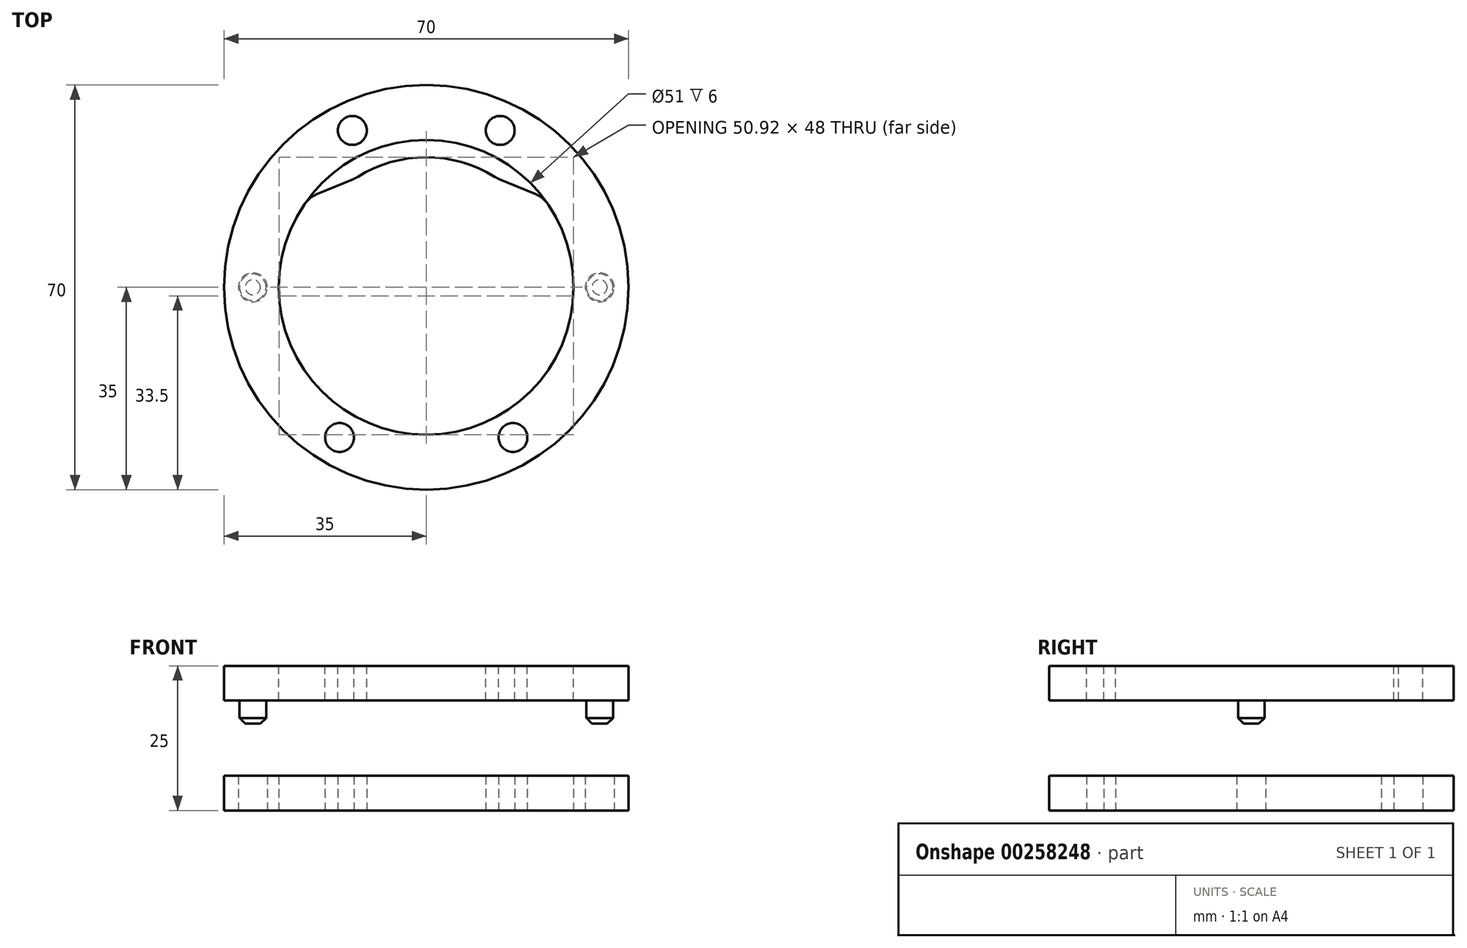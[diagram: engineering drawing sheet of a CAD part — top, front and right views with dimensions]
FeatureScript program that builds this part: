
annotation { "Feature Type Name" : "Feature", "Feature Type Description" : "" }
export const myFeature = defineFeature(function(context is Context, id is Id, definition is map)
    precondition{}
    {
        {
            var Q0;
            Q0=qCreatedBy(makeId("Top.planeOp"),FACE);
            var sketch = newSketch(context, id + "F0", { "sketchPlane" : qUnion([Q0])});
            skCircle(sketch, "E0", {"center": v(0, 0) * mm, "radius": 35 * mm});
            skArc(sketch, "E1", {"start": v(-21.1, 14.33) * mm, "mid": v(0, -25.5) * mm, "end": v(21.1, 14.33) * mm});
            skCircle(sketch, "E2", {"center": v(-15, 25.98) * mm, "radius": 2.5 * mm, "construction": true});
            skCircle(sketch, "E3", {"center": v(0, 0) * mm, "radius": 30 * mm, "construction": true});
            skCircle(sketch, "E4.1.0", {"center": v(-30, 0) * mm, "radius": 2.5 * mm});
            skCircle(sketch, "E4.2.0", {"center": v(-15, -25.98) * mm, "radius": 2.5 * mm});
            skCircle(sketch, "E5.1.3.0", {"center": v(15, -25.98) * mm, "radius": 2.5 * mm});
            skCircle(sketch, "E5.1.4.0", {"center": v(30, 0) * mm, "radius": 2.5 * mm});
            skCircle(sketch, "E5.1.5.0", {"center": v(15, 25.98) * mm, "radius": 2.5 * mm, "construction": true});
            skLineSegment(sketch, "E6", {"start": v(-18.87, 16.14) * mm, "end": v(-12.63, 18.72) * mm});
            skArc(sketch, "E7", {"start": v(11.9, 19.1) * mm, "mid": v(0, 22.5) * mm, "end": v(-11.9, 19.1) * mm});
            skLineSegment(sketch, "E8", {"start": v(18.87, 16.14) * mm, "end": v(12.63, 18.72) * mm});
            skPoint(sketch, "E9.visualSharp", {"position": v(20.17, 15.6) * mm});
            skArc(sketch, "E9.filletArc", {"start": v(21.1, 14.33) * mm, "mid": v(20.11, 15.4) * mm, "end": v(18.87, 16.14) * mm});
            skPoint(sketch, "E10.visualSharp", {"position": v(-12.23, 18.89) * mm});
            skArc(sketch, "E10.filletArc", {"start": v(-12.63, 18.72) * mm, "mid": v(-12.26, 18.9) * mm, "end": v(-11.9, 19.1) * mm});
            skPoint(sketch, "E11.visualSharp", {"position": v(-20.17, 15.6) * mm});
            skArc(sketch, "E11.filletArc", {"start": v(-18.87, 16.14) * mm, "mid": v(-20.11, 15.4) * mm, "end": v(-21.1, 14.33) * mm});
            skPoint(sketch, "E12.visualSharp", {"position": v(12.23, 18.89) * mm});
            skArc(sketch, "E12.filletArc", {"start": v(11.9, 19.1) * mm, "mid": v(12.26, 18.9) * mm, "end": v(12.63, 18.72) * mm});
            skCircle(sketch, "E13", {"center": v(12.78, 27.14) * mm, "radius": 2.5 * mm});
            skCircle(sketch, "E14", {"center": v(-12.78, 27.14) * mm, "radius": 2.5 * mm});
            skSolve(sketch);
        }
        {
            var Q0;
            Q0 = qSketchRegion(id + "F0", true);
            extrude(context, id + "F1", {"entities" : qUnion([Q0]), "depth" : 6 * mm});
        }
        {
            var Q0;
            Q0=qCreatedBy(makeId("Top.planeOp"),FACE);
            cPlane(context, id + "F2", {"entities" : qUnion([Q0]), "cplaneType" : CPlaneType.OFFSET, "offset" : 25 * mm, "width" : 150 * mm, "height" : 150 * mm});
        }
        {
            var Q0;
            Q0=qCreatedBy(id+"F2.planeOp",FACE);
            var sketch = newSketch(context, id + "F3", { "sketchPlane" : qUnion([Q0])});
            skCircle(sketch, "E15.0", {"center": v(0, 0) * mm, "radius": 25.5 * mm});
            skCircle(sketch, "E15.1", {"center": v(0, 0) * mm, "radius": 35 * mm});
            skCircle(sketch, "E16.3", {"center": v(-15, -25.98) * mm, "radius": 2.5 * mm});
            skCircle(sketch, "E17.0", {"center": v(12.78, 27.14) * mm, "radius": 2.5 * mm});
            skCircle(sketch, "E17.1", {"center": v(-12.78, 27.14) * mm, "radius": 2.5 * mm});
            skCircle(sketch, "E18.0", {"center": v(15, -25.98) * mm, "radius": 2.5 * mm});
            skSolve(sketch);
        }
        {
            var Q0;
            Q0 = qSketchRegion(id + "F3", true);
            extrude(context, id + "F4", {"entities" : qUnion([Q0]), "oppositeDirection" : true, "depth" : 6 * mm});
        }
        {
            var Q0;
            Q0=makeQuery(id+"F4.opExtrude","CAP_FACE",FACE,{"disambiguationData":[OSD([sQuery(id+"F3.wireOp",EDGE,"E15.0"),sQuery(id+"F3.wireOp",EDGE,"E15.1")])],"isStart":false});
            var sketch = newSketch(context, id + "F5", { "sketchPlane" : qUnion([Q0])});
            skCircle(sketch, "E19.0", {"center": v(30, 0) * mm, "radius": 2.5 * mm, "construction": true});
            skCircle(sketch, "E19.1", {"center": v(-30, 0) * mm, "radius": 2.5 * mm, "construction": true});
            skCircle(sketch, "E20.0", {"center": v(-30, 0) * mm, "radius": 2.3 * mm});
            skCircle(sketch, "E21.0", {"center": v(30, 0) * mm, "radius": 2.3 * mm});
            skSolve(sketch);
        }
        {
            var Q0;
            Q0 = qSketchRegion(id + "F5", true);
            extrude(context, id + "F6", {"entities" : qUnion([Q0]), "operationType" : NewBodyOperationType.ADD, "depth" : 4 * mm});
        }
        {
            var Q0;
            Q0=makeQuery(id+"F6.opExtrude","CAP_FACE",FACE,{"disambiguationData":[OSD([sQuery(id+"F5.wireOp",EDGE,"E20.0")])],"isStart":false});
            var Q1;
            Q1=makeQuery(id+"F6.opExtrude","CAP_FACE",FACE,{"disambiguationData":[OSD([sQuery(id+"F5.wireOp",EDGE,"E21.0")])],"isStart":false});
            chamfer(context, id + "F7", {"entities" : qUnion([Q0, Q1]), "width" : 1 * mm, "tangentPropagation" : true});
        }
    });
